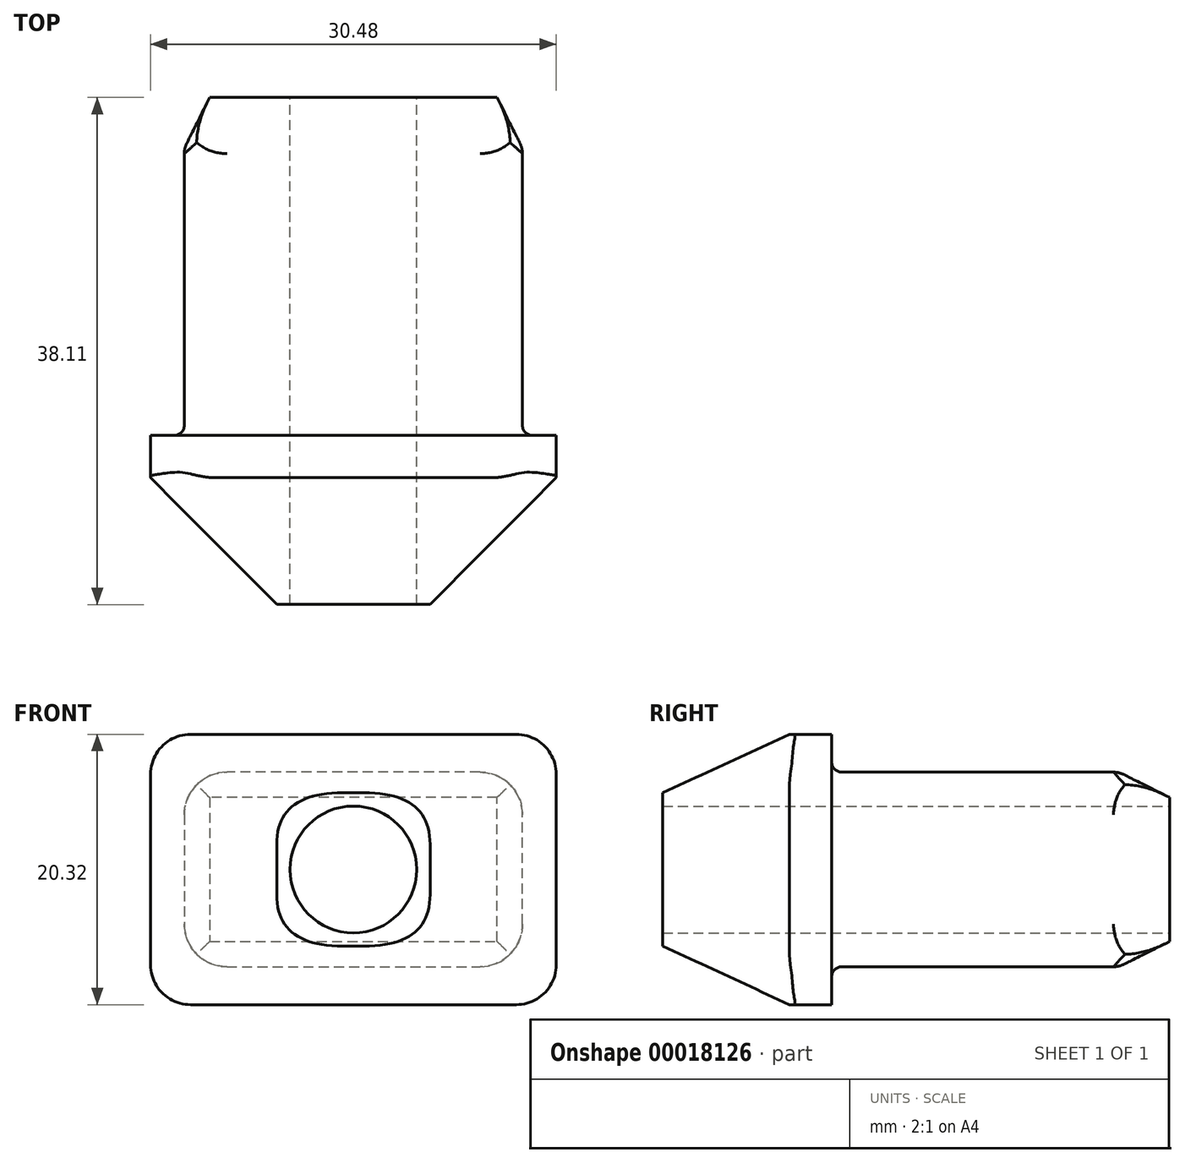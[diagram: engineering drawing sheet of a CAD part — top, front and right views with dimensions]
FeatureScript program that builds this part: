
annotation { "Feature Type Name" : "Feature", "Feature Type Description" : "" }
export const myFeature = defineFeature(function(context is Context, id is Id, definition is map)
    precondition{}
    {
        {
            var Q0;
            Q0=qCreatedBy(makeId("Front.planeOp"),FACE);
            var sketch = newSketch(context, id + "F0", { "sketchPlane" : qUnion([Q0])});
            skLineSegment(sketch, "E0.bottom", {"start": v(0, 0) * mm, "end": v(30.48, 0) * mm});
            skLineSegment(sketch, "E0.top", {"start": v(0, 20.32) * mm, "end": v(30.48, 20.32) * mm});
            skLineSegment(sketch, "E0.left", {"start": v(0, 0) * mm, "end": v(0, 20.32) * mm});
            skLineSegment(sketch, "E0.right", {"start": v(30.48, 0) * mm, "end": v(30.48, 20.32) * mm});
            skSolve(sketch);
        }
        {
            var Q0;
            Q0=makeQuery(id+"F0.imprint","IMPRINT",FACE,{"disambiguationData":[TD([[makeQuery(id+"F0.imprint","IMPRINT",EDGE,{"derivedFrom":sQuery(id+"F0.wireOp",EDGE,"E0.bottom")}),1.0]])]});
            extrude(context, id + "F1", {"entities" : qUnion([Q0]), "oppositeDirection" : true, "depth" : 3.17 * mm});
        }
        {
            var Q0;
            Q0=makeQuery(id+"F1.opExtrude","CAP_FACE",FACE,{"disambiguationData":[OSD([sQuery(id+"F0.wireOp",EDGE,"E0.bottom"),sQuery(id+"F0.wireOp",EDGE,"E0.top"),sQuery(id+"F0.wireOp",EDGE,"E0.left"),sQuery(id+"F0.wireOp",EDGE,"E0.right")])],"isStart":false});
            var sketch = newSketch(context, id + "F2", { "sketchPlane" : qUnion([Q0])});
            skLineSegment(sketch, "E1.bottom", {"start": v(-2.53, 2.85) * mm, "end": v(-27.95, 2.85) * mm});
            skLineSegment(sketch, "E1.top", {"start": v(-2.53, 17.47) * mm, "end": v(-27.95, 17.47) * mm});
            skLineSegment(sketch, "E1.left", {"start": v(-2.53, 2.85) * mm, "end": v(-2.53, 17.47) * mm});
            skLineSegment(sketch, "E1.right", {"start": v(-27.95, 2.85) * mm, "end": v(-27.95, 17.47) * mm});
            skSolve(sketch);
        }
        {
            var Q0;
            Q0=makeQuery(id+"F2.imprint","IMPRINT",FACE,{"disambiguationData":[TD([[makeQuery(id+"F2.imprint","IMPRINT",EDGE,{"derivedFrom":sQuery(id+"F2.wireOp",EDGE,"E1.bottom")}),-1.0]])]});
            extrude(context, id + "F3", {"entities" : qUnion([Q0]), "operationType" : NewBodyOperationType.ADD, "depth" : 25.4 * mm});
        }
        {
            var Q0;
            Q0=makeQuery(id+"F3.opExtrude","CAP_FACE",FACE,{"disambiguationData":[OSD([sQuery(id+"F2.wireOp",EDGE,"E1.bottom"),sQuery(id+"F2.wireOp",EDGE,"E1.top"),sQuery(id+"F2.wireOp",EDGE,"E1.left"),sQuery(id+"F2.wireOp",EDGE,"E1.right")])],"isStart":false});
            var sketch = newSketch(context, id + "F4", { "sketchPlane" : qUnion([Q0])});
            skCircle(sketch, "E2", {"center": v(-15.24, 10.16) * mm, "radius": 4.76 * mm});
            skLineSegment(sketch, "E3", {"start": v(-30.48, 10.16) * mm, "end": v(0, 10.16) * mm, "construction": true});
            skLineSegment(sketch, "E4", {"start": v(-15.24, 20.32) * mm, "end": v(-15.24, 0) * mm, "construction": true});
            skSolve(sketch);
        }
        {
            var Q0;
            Q0=makeQuery(id+"F4.imprint","IMPRINT",FACE,{"disambiguationData":[TD([[makeQuery(id+"F4.imprint","IMPRINT",EDGE,{"derivedFrom":sQuery(id+"F4.wireOp",EDGE,"E2")}),1.0]])]});
            extrude(context, id + "F5", {"entities" : qUnion([Q0]), "operationType" : NewBodyOperationType.REMOVE, "oppositeDirection" : true, "depth" : 12.7 * mm});
        }
        {
            var Q0;
            Q0=makeQuery(id+"F3.opExtrude","SWEPT_FACE",FACE,{"disambiguationData":[OSD([sQuery(id+"F2.wireOp",EDGE,"E1.top")])]});
            var sketch = newSketch(context, id + "F6", { "sketchPlane" : qUnion([Q0])});
            skLineSegment(sketch, "E5", {"start": v(2.53, 24.77) * mm, "end": v(4.44, 28.57) * mm});
            skSolve(sketch);
        }
        {
            var Q0;
            {var subQ2=sQuery(id+"F6.wireOp",EDGE,"E5");Q0=makeQuery(id+"F6.imprint","IMPRINT",FACE,{"disambiguationData":[TD([[makeQuery(id+"F6.imprint","IMPRINT",EDGE,{"derivedFrom":subQ2}),1.0]])]});}
            var Q1;
            Q1=makeQuery(id+"F3.opExtrude","CAP_EDGE",EDGE,{"disambiguationData":[OSD([sQuery(id+"F2.wireOp",EDGE,"E1.left")])],"isStart":false});
            var Q2;
            Q2=makeQuery(id+"F3.opExtrude","CAP_EDGE",EDGE,{"disambiguationData":[OSD([sQuery(id+"F2.wireOp",EDGE,"E1.bottom")])],"isStart":false});
            var Q3;
            Q3=makeQuery(id+"F3.opExtrude","CAP_EDGE",EDGE,{"disambiguationData":[OSD([sQuery(id+"F2.wireOp",EDGE,"E1.right")])],"isStart":false});
            var Q4;
            Q4=makeQuery(id+"F3.opExtrude","CAP_EDGE",EDGE,{"disambiguationData":[OSD([sQuery(id+"F2.wireOp",EDGE,"E1.top")])],"isStart":false});
            sweep(context, id + "F7", {"operationType" : NewBodyOperationType.REMOVE, "profiles" : qUnion([Q0]), "path" : qUnion([Q1, Q2, Q3, Q4])});
        }
        {
            var Q0;
            Q0=makeQuery(id+"F3.opExtrude","SWEPT_EDGE",EDGE,{"disambiguationData":[OSD([sQuery(id+"F2.wireOp",EDGE,"E1.top"),sQuery(id+"F2.wireOp",EDGE,"E1.right")])]});
            var Q1;
            Q1=makeQuery(id+"F3.opExtrude","SWEPT_EDGE",EDGE,{"disambiguationData":[OSD([sQuery(id+"F2.wireOp",EDGE,"E1.bottom"),sQuery(id+"F2.wireOp",EDGE,"E1.right")])]});
            var Q2;
            Q2=makeQuery(id+"F3.opExtrude","SWEPT_EDGE",EDGE,{"disambiguationData":[OSD([sQuery(id+"F2.wireOp",EDGE,"E1.top"),sQuery(id+"F2.wireOp",EDGE,"E1.left")])]});
            var Q3;
            Q3=makeQuery(id+"F3.opExtrude","SWEPT_EDGE",EDGE,{"disambiguationData":[OSD([sQuery(id+"F2.wireOp",EDGE,"E1.bottom"),sQuery(id+"F2.wireOp",EDGE,"E1.left")])]});
            fillet(context, id + "F8", {"entities" : qUnion([Q0, Q1, Q2, Q3]), "radius" : 3.2 * mm, "tangentPropagation" : true, "allowEdgeOverflow" : false});
        }
        {
            var Q0;
            Q0=makeQuery(id+"F5.boolean.opBoolean","COPY",FACE,{"derivedFrom":makeQuery(id+"F5.opExtrude","CAP_FACE",FACE,{"disambiguationData":[OSD([sQuery(id+"F4.wireOp",EDGE,"E2")])],"isStart":false})});
            var sketch = newSketch(context, id + "F9", { "sketchPlane" : qUnion([Q0])});
            skCircle(sketch, "E6", {"center": v(-15.24, 10.16) * mm, "radius": 4.76 * mm});
            skSolve(sketch);
        }
        {
            var Q0;
            Q0=makeQuery(id+"F3.opExtrude","CAP_EDGE",EDGE,{"disambiguationData":[OSD([sQuery(id+"F2.wireOp",EDGE,"E1.bottom")])],"isStart":true});
            var Q1;
            Q1=makeQuery(id+"F8.opFillet","BLEND_EDGE",EDGE,{"blendedFrom":[makeQuery(id+"F3.opExtrude","SWEPT_EDGE",EDGE,{"disambiguationData":[OSD([sQuery(id+"F2.wireOp",EDGE,"E1.bottom"),sQuery(id+"F2.wireOp",EDGE,"E1.left")])]}),makeQuery(id+"F1.opExtrude","CAP_FACE",FACE,{"disambiguationData":[OSD([sQuery(id+"F0.wireOp",EDGE,"E0.bottom"),sQuery(id+"F0.wireOp",EDGE,"E0.top"),sQuery(id+"F0.wireOp",EDGE,"E0.left"),sQuery(id+"F0.wireOp",EDGE,"E0.right")])],"isStart":false})],"blendedInto":[makeQuery(id+"F1.opExtrude","CAP_FACE",FACE,{"disambiguationData":[OSD([sQuery(id+"F0.wireOp",EDGE,"E0.bottom"),sQuery(id+"F0.wireOp",EDGE,"E0.top"),sQuery(id+"F0.wireOp",EDGE,"E0.left"),sQuery(id+"F0.wireOp",EDGE,"E0.right")])],"isStart":false})]});
            var Q2;
            Q2=makeQuery(id+"F3.opExtrude","CAP_EDGE",EDGE,{"disambiguationData":[OSD([sQuery(id+"F2.wireOp",EDGE,"E1.left")])],"isStart":true});
            var Q3;
            Q3=makeQuery(id+"F8.opFillet","BLEND_EDGE",EDGE,{"blendedFrom":[makeQuery(id+"F3.opExtrude","SWEPT_EDGE",EDGE,{"disambiguationData":[OSD([sQuery(id+"F2.wireOp",EDGE,"E1.top"),sQuery(id+"F2.wireOp",EDGE,"E1.left")])]}),makeQuery(id+"F1.opExtrude","CAP_FACE",FACE,{"disambiguationData":[OSD([sQuery(id+"F0.wireOp",EDGE,"E0.bottom"),sQuery(id+"F0.wireOp",EDGE,"E0.top"),sQuery(id+"F0.wireOp",EDGE,"E0.left"),sQuery(id+"F0.wireOp",EDGE,"E0.right")])],"isStart":false})],"blendedInto":[makeQuery(id+"F1.opExtrude","CAP_FACE",FACE,{"disambiguationData":[OSD([sQuery(id+"F0.wireOp",EDGE,"E0.bottom"),sQuery(id+"F0.wireOp",EDGE,"E0.top"),sQuery(id+"F0.wireOp",EDGE,"E0.left"),sQuery(id+"F0.wireOp",EDGE,"E0.right")])],"isStart":false})]});
            var Q4;
            Q4=makeQuery(id+"F3.opExtrude","CAP_EDGE",EDGE,{"disambiguationData":[OSD([sQuery(id+"F2.wireOp",EDGE,"E1.top")])],"isStart":true});
            var Q5;
            Q5=makeQuery(id+"F8.opFillet","BLEND_EDGE",EDGE,{"blendedFrom":[makeQuery(id+"F3.opExtrude","SWEPT_EDGE",EDGE,{"disambiguationData":[OSD([sQuery(id+"F2.wireOp",EDGE,"E1.top"),sQuery(id+"F2.wireOp",EDGE,"E1.right")])]}),makeQuery(id+"F1.opExtrude","CAP_FACE",FACE,{"disambiguationData":[OSD([sQuery(id+"F0.wireOp",EDGE,"E0.bottom"),sQuery(id+"F0.wireOp",EDGE,"E0.top"),sQuery(id+"F0.wireOp",EDGE,"E0.left"),sQuery(id+"F0.wireOp",EDGE,"E0.right")])],"isStart":false})],"blendedInto":[makeQuery(id+"F1.opExtrude","CAP_FACE",FACE,{"disambiguationData":[OSD([sQuery(id+"F0.wireOp",EDGE,"E0.bottom"),sQuery(id+"F0.wireOp",EDGE,"E0.top"),sQuery(id+"F0.wireOp",EDGE,"E0.left"),sQuery(id+"F0.wireOp",EDGE,"E0.right")])],"isStart":false})]});
            var Q6;
            Q6=makeQuery(id+"F3.opExtrude","CAP_EDGE",EDGE,{"disambiguationData":[OSD([sQuery(id+"F2.wireOp",EDGE,"E1.right")])],"isStart":true});
            var Q7;
            Q7=makeQuery(id+"F8.opFillet","BLEND_EDGE",EDGE,{"blendedFrom":[makeQuery(id+"F3.opExtrude","SWEPT_EDGE",EDGE,{"disambiguationData":[OSD([sQuery(id+"F2.wireOp",EDGE,"E1.bottom"),sQuery(id+"F2.wireOp",EDGE,"E1.right")])]}),makeQuery(id+"F1.opExtrude","CAP_FACE",FACE,{"disambiguationData":[OSD([sQuery(id+"F0.wireOp",EDGE,"E0.bottom"),sQuery(id+"F0.wireOp",EDGE,"E0.top"),sQuery(id+"F0.wireOp",EDGE,"E0.left"),sQuery(id+"F0.wireOp",EDGE,"E0.right")])],"isStart":false})],"blendedInto":[makeQuery(id+"F1.opExtrude","CAP_FACE",FACE,{"disambiguationData":[OSD([sQuery(id+"F0.wireOp",EDGE,"E0.bottom"),sQuery(id+"F0.wireOp",EDGE,"E0.top"),sQuery(id+"F0.wireOp",EDGE,"E0.left"),sQuery(id+"F0.wireOp",EDGE,"E0.right")])],"isStart":false})]});
            fillet(context, id + "F10", {"entities" : qUnion([Q0, Q1, Q2, Q3, Q4, Q5, Q6, Q7]), "radius" : 0.75 * mm, "tangentPropagation" : true, "allowEdgeOverflow" : false});
        }
        {
            var Q0;
            Q0=makeQuery(id+"F1.opExtrude","CAP_FACE",FACE,{"disambiguationData":[OSD([sQuery(id+"F0.wireOp",EDGE,"E0.bottom"),sQuery(id+"F0.wireOp",EDGE,"E0.top"),sQuery(id+"F0.wireOp",EDGE,"E0.left"),sQuery(id+"F0.wireOp",EDGE,"E0.right")])],"isStart":true});
            var sketch = newSketch(context, id + "F11", { "sketchPlane" : qUnion([Q0])});
            skLineSegment(sketch, "E7", {"start": v(0, 10.16) * mm, "end": v(30.48, 10.16) * mm, "construction": true});
            skLineSegment(sketch, "E8", {"start": v(15.24, 0) * mm, "end": v(15.24, 20.32) * mm, "construction": true});
            skLineSegment(sketch, "E9", {"start": v(30.48, 20.32) * mm, "end": v(0, 0) * mm, "construction": true});
            skLineSegment(sketch, "E10", {"start": v(0, 20.32) * mm, "end": v(30.48, 0) * mm, "construction": true});
            skSolve(sketch);
        }
        {
            var Q0;
            {var subQ0=sQuery(id+"F0.wireOp",EDGE,"E0.bottom");Q0=makeQuery(id+"F11.imprint","IMPRINT",FACE,{"disambiguationData":[TD([[makeQuery(id+"F11.imprint","IMPRINT",EDGE,{"derivedFrom":makeQuery(id+"F1.opExtrude","CAP_EDGE",EDGE,{"disambiguationData":[OSD([subQ0])],"isStart":true})}),1.0]])]});}
            cPlane(context, id + "F12", {"entities" : qUnion([Q0]), "cplaneType" : CPlaneType.OFFSET, "offset" : 9.53 * mm, "width" : 150 * mm, "height" : 150 * mm});
        }
        {
            var Q0;
            Q0=qCreatedBy(id+"F12.planeOp",FACE);
            var sketch = newSketch(context, id + "F13", { "sketchPlane" : qUnion([Q0])});
            skCircle(sketch, "E11", {"center": v(15.24, 10.16) * mm, "radius": 5.76 * mm, "construction": true});
            skLineSegment(sketch, "E12.bottom", {"start": v(9.48, 15.92) * mm, "end": v(21, 15.92) * mm});
            skLineSegment(sketch, "E12.top", {"start": v(9.48, 4.4) * mm, "end": v(21, 4.4) * mm});
            skLineSegment(sketch, "E12.left", {"start": v(9.48, 15.92) * mm, "end": v(9.48, 4.4) * mm});
            skLineSegment(sketch, "E12.right", {"start": v(21, 15.92) * mm, "end": v(21, 4.4) * mm});
            skSolve(sketch);
        }
        {
            var Q1;
            Q1=makeQuery(id+"F11.imprint","IMPRINT",FACE,{"disambiguationData":[TD([[makeQuery(id+"F11.imprint","IMPRINT",EDGE,{"derivedFrom":makeQuery(id+"F1.opExtrude","CAP_EDGE",EDGE,{"disambiguationData":[OSD([sQuery(id+"F0.wireOp",EDGE,"E0.bottom")])],"isStart":true})}),1.0]])]});
            var Q2;
            Q2=makeQuery(id+"F13.imprint","IMPRINT",FACE,{"disambiguationData":[TD([[makeQuery(id+"F13.imprint","IMPRINT",EDGE,{"derivedFrom":sQuery(id+"F13.wireOp",EDGE,"E12.bottom")}),-1.0]])]});
            loft(context, id + "F14", {"operationType" : NewBodyOperationType.ADD, "sheetProfilesArray" : [{ "sheetProfileEntities" : qUnion([Q1]) }, { "sheetProfileEntities" : qUnion([Q2]) }]});
        }
        {
            var Q0;
            Q0=makeQuery(id+"F9.imprint","IMPRINT",FACE,{"disambiguationData":[TD([[makeQuery(id+"F9.imprint","IMPRINT",EDGE,{"derivedFrom":sQuery(id+"F9.wireOp",EDGE,"E6")}),1.0]])]});
            extrude(context, id + "F15", {"entities" : qUnion([Q0]), "operationType" : NewBodyOperationType.REMOVE, "endBound" : BoundingType.THROUGH_ALL, "oppositeDirection" : true, "depth" : 2 * mm});
        }
        {
            var Q0;
            Q0=makeQuery(id+"F14.opLoft","SWEPT_EDGE",EDGE,{"disambiguationData":[OSD([sQuery(id+"F0.wireOp",EDGE,"E0.top"),sQuery(id+"F0.wireOp",EDGE,"E0.left"),sQuery(id+"F13.wireOp",EDGE,"E12.bottom"),sQuery(id+"F13.wireOp",EDGE,"E12.left")])]});
            var Q1;
            Q1=makeQuery(id+"F14.opLoft","SWEPT_EDGE",EDGE,{"disambiguationData":[OSD([sQuery(id+"F0.wireOp",EDGE,"E0.top"),sQuery(id+"F0.wireOp",EDGE,"E0.right"),sQuery(id+"F13.wireOp",EDGE,"E12.bottom"),sQuery(id+"F13.wireOp",EDGE,"E12.right")])]});
            var Q2;
            Q2=makeQuery(id+"F14.opLoft","SWEPT_EDGE",EDGE,{"disambiguationData":[OSD([sQuery(id+"F0.wireOp",EDGE,"E0.bottom"),sQuery(id+"F0.wireOp",EDGE,"E0.right"),sQuery(id+"F13.wireOp",EDGE,"E12.top"),sQuery(id+"F13.wireOp",EDGE,"E12.right")])]});
            var Q3;
            Q3=makeQuery(id+"F14.opLoft","SWEPT_EDGE",EDGE,{"disambiguationData":[OSD([sQuery(id+"F0.wireOp",EDGE,"E0.bottom"),sQuery(id+"F0.wireOp",EDGE,"E0.left"),sQuery(id+"F13.wireOp",EDGE,"E12.top"),sQuery(id+"F13.wireOp",EDGE,"E12.left")])]});
            fillet(context, id + "F16", {"entities" : qUnion([Q0, Q1, Q2, Q3]), "radius" : 5 * mm, "rho" : 0.5, "crossSection" : FilletCrossSection.CONIC, "allowEdgeOverflow" : false});
        }
        {
            var Q0;
            {var subQ0=sQuery(id+"F2.wireOp",EDGE,"E1.top");Q0=makeQuery(id+"F8.opFillet","BLEND_EDGE",EDGE,{"blendedFrom":[makeQuery(id+"F3.opExtrude","SWEPT_EDGE",EDGE,{"disambiguationData":[OSD([subQ0,sQuery(id+"F2.wireOp",EDGE,"E1.right")])]}),makeQuery(id+"F7.boolean.opBoolean","COPY",FACE,{"derivedFrom":makeQuery(id+"F7.opSweep","SWEPT_FACE",FACE,{"disambiguationData":[OSD([subQ0,sQuery(id+"F6.wireOp",EDGE,"E5")])]})})],"blendedInto":[makeQuery(id+"F7.boolean.opBoolean","COPY",FACE,{"derivedFrom":makeQuery(id+"F7.opSweep","SWEPT_FACE",FACE,{"disambiguationData":[OSD([subQ0,sQuery(id+"F6.wireOp",EDGE,"E5")])]})})]});}
            var Q1;
            {var subQ0=sQuery(id+"F2.wireOp",EDGE,"E1.right");Q1=makeQuery(id+"F8.opFillet","BLEND_EDGE",EDGE,{"blendedFrom":[makeQuery(id+"F3.opExtrude","SWEPT_EDGE",EDGE,{"disambiguationData":[OSD([sQuery(id+"F2.wireOp",EDGE,"E1.top"),subQ0])]}),makeQuery(id+"F7.boolean.opBoolean","COPY",FACE,{"derivedFrom":makeQuery(id+"F7.opSweep","SWEPT_FACE",FACE,{"disambiguationData":[OSD([subQ0,sQuery(id+"F6.wireOp",EDGE,"E5")])]})})],"blendedInto":[makeQuery(id+"F7.boolean.opBoolean","COPY",FACE,{"derivedFrom":makeQuery(id+"F7.opSweep","SWEPT_FACE",FACE,{"disambiguationData":[OSD([subQ0,sQuery(id+"F6.wireOp",EDGE,"E5")])]})})]});}
            var Q2;
            {var subQ0=sQuery(id+"F2.wireOp",EDGE,"E1.right");Q2=makeQuery(id+"F8.opFillet","BLEND_EDGE",EDGE,{"blendedFrom":[makeQuery(id+"F3.opExtrude","SWEPT_EDGE",EDGE,{"disambiguationData":[OSD([sQuery(id+"F2.wireOp",EDGE,"E1.bottom"),subQ0])]}),makeQuery(id+"F7.boolean.opBoolean","COPY",FACE,{"derivedFrom":makeQuery(id+"F7.opSweep","SWEPT_FACE",FACE,{"disambiguationData":[OSD([subQ0,sQuery(id+"F6.wireOp",EDGE,"E5")])]})})],"blendedInto":[makeQuery(id+"F7.boolean.opBoolean","COPY",FACE,{"derivedFrom":makeQuery(id+"F7.opSweep","SWEPT_FACE",FACE,{"disambiguationData":[OSD([subQ0,sQuery(id+"F6.wireOp",EDGE,"E5")])]})})]});}
            var Q3;
            {var subQ0=sQuery(id+"F2.wireOp",EDGE,"E1.bottom");Q3=makeQuery(id+"F8.opFillet","BLEND_EDGE",EDGE,{"blendedFrom":[makeQuery(id+"F3.opExtrude","SWEPT_EDGE",EDGE,{"disambiguationData":[OSD([subQ0,sQuery(id+"F2.wireOp",EDGE,"E1.right")])]}),makeQuery(id+"F7.boolean.opBoolean","COPY",FACE,{"derivedFrom":makeQuery(id+"F7.opSweep","SWEPT_FACE",FACE,{"disambiguationData":[OSD([subQ0,sQuery(id+"F6.wireOp",EDGE,"E5")])]})})],"blendedInto":[makeQuery(id+"F7.boolean.opBoolean","COPY",FACE,{"derivedFrom":makeQuery(id+"F7.opSweep","SWEPT_FACE",FACE,{"disambiguationData":[OSD([subQ0,sQuery(id+"F6.wireOp",EDGE,"E5")])]})})]});}
            var Q4;
            {var subQ0=sQuery(id+"F2.wireOp",EDGE,"E1.bottom");Q4=makeQuery(id+"F8.opFillet","BLEND_EDGE",EDGE,{"blendedFrom":[makeQuery(id+"F3.opExtrude","SWEPT_EDGE",EDGE,{"disambiguationData":[OSD([subQ0,sQuery(id+"F2.wireOp",EDGE,"E1.left")])]}),makeQuery(id+"F7.boolean.opBoolean","COPY",FACE,{"derivedFrom":makeQuery(id+"F7.opSweep","SWEPT_FACE",FACE,{"disambiguationData":[OSD([subQ0,sQuery(id+"F6.wireOp",EDGE,"E5")])]})})],"blendedInto":[makeQuery(id+"F7.boolean.opBoolean","COPY",FACE,{"derivedFrom":makeQuery(id+"F7.opSweep","SWEPT_FACE",FACE,{"disambiguationData":[OSD([subQ0,sQuery(id+"F6.wireOp",EDGE,"E5")])]})})]});}
            var Q5;
            {var subQ0=sQuery(id+"F2.wireOp",EDGE,"E1.left");Q5=makeQuery(id+"F8.opFillet","BLEND_EDGE",EDGE,{"blendedFrom":[makeQuery(id+"F3.opExtrude","SWEPT_EDGE",EDGE,{"disambiguationData":[OSD([sQuery(id+"F2.wireOp",EDGE,"E1.bottom"),subQ0])]}),makeQuery(id+"F7.boolean.opBoolean","COPY",FACE,{"derivedFrom":makeQuery(id+"F7.opSweep","SWEPT_FACE",FACE,{"disambiguationData":[OSD([subQ0,sQuery(id+"F6.wireOp",EDGE,"E5")])]})})],"blendedInto":[makeQuery(id+"F7.boolean.opBoolean","COPY",FACE,{"derivedFrom":makeQuery(id+"F7.opSweep","SWEPT_FACE",FACE,{"disambiguationData":[OSD([subQ0,sQuery(id+"F6.wireOp",EDGE,"E5")])]})})]});}
            var Q6;
            {var subQ0=sQuery(id+"F2.wireOp",EDGE,"E1.left");Q6=makeQuery(id+"F8.opFillet","BLEND_EDGE",EDGE,{"blendedFrom":[makeQuery(id+"F3.opExtrude","SWEPT_EDGE",EDGE,{"disambiguationData":[OSD([sQuery(id+"F2.wireOp",EDGE,"E1.top"),subQ0])]}),makeQuery(id+"F7.boolean.opBoolean","COPY",FACE,{"derivedFrom":makeQuery(id+"F7.opSweep","SWEPT_FACE",FACE,{"disambiguationData":[OSD([subQ0,sQuery(id+"F6.wireOp",EDGE,"E5")])]})})],"blendedInto":[makeQuery(id+"F7.boolean.opBoolean","COPY",FACE,{"derivedFrom":makeQuery(id+"F7.opSweep","SWEPT_FACE",FACE,{"disambiguationData":[OSD([subQ0,sQuery(id+"F6.wireOp",EDGE,"E5")])]})})]});}
            var Q7;
            {var subQ0=sQuery(id+"F2.wireOp",EDGE,"E1.top");Q7=makeQuery(id+"F8.opFillet","BLEND_EDGE",EDGE,{"blendedFrom":[makeQuery(id+"F3.opExtrude","SWEPT_EDGE",EDGE,{"disambiguationData":[OSD([subQ0,sQuery(id+"F2.wireOp",EDGE,"E1.left")])]}),makeQuery(id+"F7.boolean.opBoolean","COPY",FACE,{"derivedFrom":makeQuery(id+"F7.opSweep","SWEPT_FACE",FACE,{"disambiguationData":[OSD([subQ0,sQuery(id+"F6.wireOp",EDGE,"E5")])]})})],"blendedInto":[makeQuery(id+"F7.boolean.opBoolean","COPY",FACE,{"derivedFrom":makeQuery(id+"F7.opSweep","SWEPT_FACE",FACE,{"disambiguationData":[OSD([subQ0,sQuery(id+"F6.wireOp",EDGE,"E5")])]})})]});}
            fillet(context, id + "F17", {"entities" : qUnion([Q0, Q1, Q2, Q3, Q4, Q5, Q6, Q7]), "radius" : 1.75 * mm, "tangentPropagation" : true, "allowEdgeOverflow" : false});
        }
        {
            var Q0;
            Q0=makeQuery(id+"F1.opExtrude","SWEPT_EDGE",EDGE,{"disambiguationData":[OSD([sQuery(id+"F0.wireOp",EDGE,"E0.top"),sQuery(id+"F0.wireOp",EDGE,"E0.left")])]});
            var Q1;
            Q1=makeQuery(id+"F1.opExtrude","SWEPT_EDGE",EDGE,{"disambiguationData":[OSD([sQuery(id+"F0.wireOp",EDGE,"E0.bottom"),sQuery(id+"F0.wireOp",EDGE,"E0.left")])]});
            var Q2;
            Q2=makeQuery(id+"F1.opExtrude","SWEPT_EDGE",EDGE,{"disambiguationData":[OSD([sQuery(id+"F0.wireOp",EDGE,"E0.top"),sQuery(id+"F0.wireOp",EDGE,"E0.right")])]});
            var Q3;
            Q3=makeQuery(id+"F1.opExtrude","SWEPT_EDGE",EDGE,{"disambiguationData":[OSD([sQuery(id+"F0.wireOp",EDGE,"E0.bottom"),sQuery(id+"F0.wireOp",EDGE,"E0.right")])]});
            fillet(context, id + "F18", {"entities" : qUnion([Q0, Q1, Q2, Q3]), "radius" : 3 * mm, "tangentPropagation" : true, "allowEdgeOverflow" : false});
        }
    });
